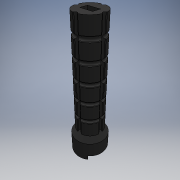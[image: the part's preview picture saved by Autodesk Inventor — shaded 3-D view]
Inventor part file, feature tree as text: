
AUTODESK INVENTOR PART (.ipt)
format: ipt  version: 2018 (Build 220112000, 112)  size: 685,568 bytes
history: native  units: mm
features: sketch x5, extrude x4, other x1, fillet x1
ambient origin geometry x8: Origin, YZ Plane, XZ Plane, XY Plane, X Axis, Y Axis, Z Axis, Center Point
bodies: Body1 (feature_tree)
feature tree (11):
  other  "Rotace3"
  extrude  "Vysunutí7"  Depth=25.0mm
  sketch  "Náčrt11"
  extrude  "Vysunutí8"  Depth=1.5mm
  extrude  "Vysunutí9"  Depth=1.5mm
  fillet  "Zaoblení4"  Radius=1.5mm
  extrude  "Vysunutí10"  Depth=1.5mm
  sketch  "Náčrt6"
  sketch  "Náčrt10"
  sketch  "Náčrt12"
  sketch  "Náčrt13"
